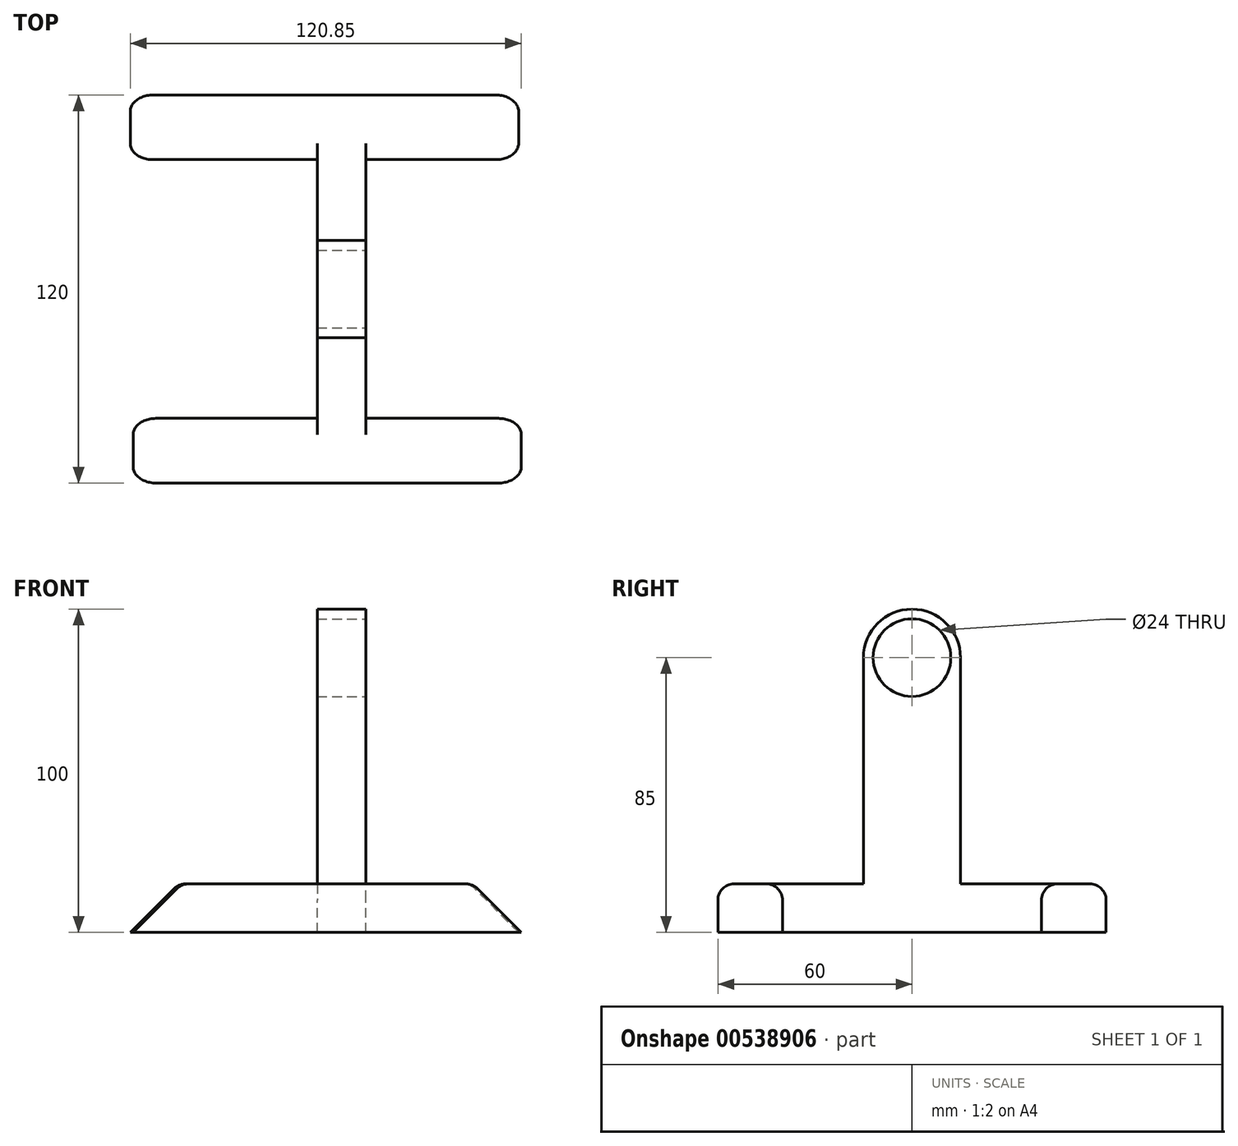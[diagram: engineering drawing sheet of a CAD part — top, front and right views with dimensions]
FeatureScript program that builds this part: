
annotation { "Feature Type Name" : "Feature", "Feature Type Description" : "" }
export const myFeature = defineFeature(function(context is Context, id is Id, definition is map)
    precondition{}
    {
        {
            var Q0;
            Q0=qCreatedBy(makeId("Front.planeOp"),FACE);
            var sketch = newSketch(context, id + "F0", { "sketchPlane" : qUnion([Q0])});
            skLineSegment(sketch, "E0", {"start": v(-49.17, 0) * mm, "end": v(10.83, 0) * mm});
            skLineSegment(sketch, "E1", {"start": v(-49.17, 0) * mm, "end": v(-64.17, 0) * mm});
            skLineSegment(sketch, "E2", {"start": v(10.83, 0) * mm, "end": v(25.83, 0) * mm});
            skLineSegment(sketch, "E3", {"start": v(-49.17, -15) * mm, "end": v(10.83, -15) * mm});
            skLineSegment(sketch, "E4", {"start": v(-49.17, -15) * mm, "end": v(-79.17, -15) * mm});
            skLineSegment(sketch, "E5", {"start": v(10.83, -15) * mm, "end": v(40.83, -15) * mm});
            skLineSegment(sketch, "E6", {"start": v(-64.17, 0) * mm, "end": v(-79.17, -15) * mm});
            skLineSegment(sketch, "E7", {"start": v(25.83, 0) * mm, "end": v(40.83, -15) * mm});
            skLineSegment(sketch, "E8", {"start": v(-49.17, 0) * mm, "end": v(-19.17, 0) * mm});
            skLineSegment(sketch, "E9", {"start": v(-19.17, 0) * mm, "end": v(10.83, 0) * mm});
            skSolve(sketch);
        }
        {
            var Q0;
            Q0 = qSketchRegion(id + "F0", true);
            extrude(context, id + "F1", {"entities" : qUnion([Q0]), "depth" : 20 * mm, "offsetDistance" : 25 * mm});
        }
        {
            var Q0;
            Q0=makeQuery(id+"F1.opExtrude","CAP_FACE",FACE,{"disambiguationData":[OSD([sQuery(id+"F0.wireOp",EDGE,"E0"),sQuery(id+"F0.wireOp",EDGE,"E1"),sQuery(id+"F0.wireOp",EDGE,"E2"),sQuery(id+"F0.wireOp",EDGE,"E3"),sQuery(id+"F0.wireOp",EDGE,"E4"),sQuery(id+"F0.wireOp",EDGE,"E5"),sQuery(id+"F0.wireOp",EDGE,"E6"),sQuery(id+"F0.wireOp",EDGE,"E7")])],"isStart":true});
            var sketch = newSketch(context, id + "F2", { "sketchPlane" : qUnion([Q0])});
            skLineSegment(sketch, "E10.bottom", {"start": v(22.23, -15) * mm, "end": v(7.23, -15) * mm});
            skLineSegment(sketch, "E10.top", {"start": v(22.23, 0) * mm, "end": v(7.23, 0) * mm});
            skLineSegment(sketch, "E10.left", {"start": v(22.23, -15) * mm, "end": v(22.23, 0) * mm});
            skLineSegment(sketch, "E10.right", {"start": v(7.23, -15) * mm, "end": v(7.23, 0) * mm});
            skPoint(sketch, "E10.middle", {"position": v(14.73, -7.5) * mm});
            skSolve(sketch);
        }
        {
            var Q0;
            Q0 = qSketchRegion(id + "F2", true);
            extrude(context, id + "F3", {"entities" : qUnion([Q0]), "operationType" : NewBodyOperationType.ADD, "depth" : 80 * mm, "offsetDistance" : 25 * mm});
        }
        {
            var Q0;
            Q0=makeQuery(id+"F3.opExtrude","CAP_FACE",FACE,{"disambiguationData":[OSD([sQuery(id+"F2.wireOp",EDGE,"E10.bottom"),sQuery(id+"F2.wireOp",EDGE,"E10.top"),sQuery(id+"F2.wireOp",EDGE,"E10.left"),sQuery(id+"F2.wireOp",EDGE,"E10.right")])],"isStart":false});
            var sketch = newSketch(context, id + "F4", { "sketchPlane" : qUnion([Q0])});
            skLineSegment(sketch, "E11", {"start": v(-24.98, 0) * mm, "end": v(65.02, 0) * mm});
            skLineSegment(sketch, "E12", {"start": v(65.02, 0) * mm, "end": v(80.02, -15) * mm});
            skLineSegment(sketch, "E13", {"start": v(80.02, -15) * mm, "end": v(-39.98, -15) * mm});
            skLineSegment(sketch, "E14", {"start": v(-39.98, -15) * mm, "end": v(-24.98, 0) * mm});
            skLineSegment(sketch, "E15", {"start": v(-39.98, -15) * mm, "end": v(-19.98, -15) * mm});
            skLineSegment(sketch, "E16", {"start": v(80.02, -15) * mm, "end": v(60.02, -15) * mm});
            skLineSegment(sketch, "E17", {"start": v(-19.98, -15) * mm, "end": v(60.02, -15) * mm});
            skSolve(sketch);
        }
        {
            var Q0;
            {var subQ2=sQuery(id+"F4.wireOp",EDGE,"E14");Q0=makeQuery(id+"F4.imprint","IMPRINT",FACE,{"disambiguationData":[TD([[makeQuery(id+"F4.imprint","IMPRINT",EDGE,{"derivedFrom":subQ2}),-1.0]])]});}
            var Q1;
            {var subQ1=makeQuery(id+"F3.opExtrude","CAP_EDGE",EDGE,{"disambiguationData":[OSD([sQuery(id+"F2.wireOp",EDGE,"E10.left")])],"isStart":false});Q1=makeQuery(id+"F4.imprint","IMPRINT",FACE,{"disambiguationData":[TD([[makeQuery(id+"F4.imprint","IMPRINT",EDGE,{"derivedFrom":subQ1}),1.0]])]});}
            var Q2;
            {var subQ2=sQuery(id+"F4.wireOp",EDGE,"E12");Q2=makeQuery(id+"F4.imprint","IMPRINT",FACE,{"disambiguationData":[TD([[makeQuery(id+"F4.imprint","IMPRINT",EDGE,{"derivedFrom":subQ2}),-1.0]])]});}
            extrude(context, id + "F5", {"entities" : qUnion([Q0, Q1, Q2]), "operationType" : NewBodyOperationType.ADD, "depth" : 20 * mm, "offsetDistance" : 25 * mm});
        }
        {
            var Q0;
            Q0=makeQuery(id+"F5.opExtrude","SWEPT_EDGE",EDGE,{"disambiguationData":[OSD([sQuery(id+"F4.wireOp",EDGE,"E11"),sQuery(id+"F4.wireOp",EDGE,"E12")])]});
            var Q1;
            Q1=makeQuery(id+"F5.opExtrude","SWEPT_EDGE",EDGE,{"disambiguationData":[OSD([sQuery(id+"F4.wireOp",EDGE,"E11"),sQuery(id+"F4.wireOp",EDGE,"E14")])]});
            var Q2;
            Q2=makeQuery(id+"F1.opExtrude","SWEPT_EDGE",EDGE,{"disambiguationData":[OSD([sQuery(id+"F0.wireOp",EDGE,"E1"),sQuery(id+"F0.wireOp",EDGE,"E6")])]});
            var Q3;
            Q3=makeQuery(id+"F1.opExtrude","SWEPT_EDGE",EDGE,{"disambiguationData":[OSD([sQuery(id+"F0.wireOp",EDGE,"E2"),sQuery(id+"F0.wireOp",EDGE,"E7")])]});
            var Q4;
            {var subQ0=sQuery(id+"F0.wireOp",EDGE,"E6");var subQ1=sQuery(id+"F0.wireOp",EDGE,"E2");var subQ2=sQuery(id+"F0.wireOp",EDGE,"E1");var subQ3=sQuery(id+"F0.wireOp",EDGE,"E0");Q4=makeQuery(id+"F3.boolean.opBoolean","SPLIT",EDGE,{"disambiguationData":[TD([makeQuery(id+"F1.opExtrude","SWEPT_FACE",FACE,{"disambiguationData":[OSD([subQ0])]})])],"derivedFrom":makeQuery(id+"F1.opExtrude","CAP_EDGE",EDGE,{"disambiguationData":[OSD([subQ3,subQ2,subQ1])],"isStart":true})});}
            var Q5;
            {var subQ0=sQuery(id+"F0.wireOp",EDGE,"E7");var subQ1=sQuery(id+"F0.wireOp",EDGE,"E2");var subQ2=sQuery(id+"F0.wireOp",EDGE,"E1");var subQ3=sQuery(id+"F0.wireOp",EDGE,"E0");Q5=makeQuery(id+"F3.boolean.opBoolean","SPLIT",EDGE,{"disambiguationData":[TD([makeQuery(id+"F1.opExtrude","SWEPT_FACE",FACE,{"disambiguationData":[OSD([subQ0])]})])],"derivedFrom":makeQuery(id+"F1.opExtrude","CAP_EDGE",EDGE,{"disambiguationData":[OSD([subQ3,subQ2,subQ1])],"isStart":true})});}
            var Q6;
            Q6=makeQuery(id+"F1.opExtrude","CAP_EDGE",EDGE,{"disambiguationData":[OSD([sQuery(id+"F0.wireOp",EDGE,"E7")])],"isStart":true});
            var Q7;
            Q7=makeQuery(id+"F1.opExtrude","CAP_EDGE",EDGE,{"disambiguationData":[OSD([sQuery(id+"F0.wireOp",EDGE,"E6")])],"isStart":true});
            var Q8;
            Q8=makeQuery(id+"F1.opExtrude","CAP_EDGE",EDGE,{"disambiguationData":[OSD([sQuery(id+"F0.wireOp",EDGE,"E6")])],"isStart":false});
            var Q9;
            Q9=makeQuery(id+"F1.opExtrude","CAP_EDGE",EDGE,{"disambiguationData":[OSD([sQuery(id+"F0.wireOp",EDGE,"E0"),sQuery(id+"F0.wireOp",EDGE,"E1"),sQuery(id+"F0.wireOp",EDGE,"E2")])],"isStart":false});
            var Q10;
            Q10=makeQuery(id+"F1.opExtrude","CAP_EDGE",EDGE,{"disambiguationData":[OSD([sQuery(id+"F0.wireOp",EDGE,"E7")])],"isStart":false});
            var Q11;
            {var subQ0=sQuery(id+"F4.wireOp",EDGE,"E11");Q11=makeQuery(id+"F5.boolean.opBoolean","SPLIT",EDGE,{"disambiguationData":[TD([makeQuery(id+"F3.opExtrude","SWEPT_FACE",FACE,{"disambiguationData":[OSD([sQuery(id+"F2.wireOp",EDGE,"E10.right")])]})])],"derivedFrom":makeQuery(id+"F5.opExtrude","CAP_EDGE",EDGE,{"disambiguationData":[OSD([subQ0])],"isStart":true})});}
            var Q12;
            {var subQ0=sQuery(id+"F4.wireOp",EDGE,"E11");Q12=makeQuery(id+"F5.boolean.opBoolean","SPLIT",EDGE,{"disambiguationData":[TD([makeQuery(id+"F3.opExtrude","SWEPT_FACE",FACE,{"disambiguationData":[OSD([sQuery(id+"F2.wireOp",EDGE,"E10.left")])]})])],"derivedFrom":makeQuery(id+"F5.opExtrude","CAP_EDGE",EDGE,{"disambiguationData":[OSD([subQ0])],"isStart":true})});}
            var Q13;
            Q13=makeQuery(id+"F5.opExtrude","CAP_EDGE",EDGE,{"disambiguationData":[OSD([sQuery(id+"F4.wireOp",EDGE,"E12")])],"isStart":true});
            var Q14;
            Q14=makeQuery(id+"F5.opExtrude","CAP_EDGE",EDGE,{"disambiguationData":[OSD([sQuery(id+"F4.wireOp",EDGE,"E12")])],"isStart":false});
            var Q15;
            Q15=makeQuery(id+"F5.opExtrude","CAP_EDGE",EDGE,{"disambiguationData":[OSD([sQuery(id+"F4.wireOp",EDGE,"E11")])],"isStart":false});
            var Q16;
            Q16=makeQuery(id+"F5.opExtrude","CAP_EDGE",EDGE,{"disambiguationData":[OSD([sQuery(id+"F4.wireOp",EDGE,"E14")])],"isStart":false});
            var Q17;
            Q17=makeQuery(id+"F5.opExtrude","CAP_EDGE",EDGE,{"disambiguationData":[OSD([sQuery(id+"F4.wireOp",EDGE,"E14")])],"isStart":true});
            fillet(context, id + "F6", {"entities" : qUnion([Q0, Q1, Q2, Q3, Q4, Q5, Q6, Q7, Q8, Q9, Q10, Q11, Q12, Q13, Q14, Q15, Q16, Q17]), "radius" : 5 * mm, "tangentPropagation" : true, "allowEdgeOverflow" : false});
        }
        {
            var Q0;
            Q0=makeQuery(id+"F5.boolean.opBoolean","MERGE",FACE,{"derivedFrom":[makeQuery(id+"F3.boolean.opBoolean","MERGE",FACE,{"derivedFrom":[makeQuery(id+"F1.opExtrude","SWEPT_FACE",FACE,{"disambiguationData":[OSD([sQuery(id+"F0.wireOp",EDGE,"E0"),sQuery(id+"F0.wireOp",EDGE,"E1"),sQuery(id+"F0.wireOp",EDGE,"E2")])]}),makeQuery(id+"F3.opExtrude","SWEPT_FACE",FACE,{"disambiguationData":[OSD([sQuery(id+"F2.wireOp",EDGE,"E10.top")])]})]}),makeQuery(id+"F5.opExtrude","SWEPT_FACE",FACE,{"disambiguationData":[OSD([sQuery(id+"F4.wireOp",EDGE,"E11")])]})]});
            var sketch = newSketch(context, id + "F7", { "sketchPlane" : qUnion([Q0])});
            skLineSegment(sketch, "E18.bottom", {"start": v(-7.23, 25) * mm, "end": v(-22.23, 25) * mm});
            skLineSegment(sketch, "E18.top", {"start": v(-7.23, 55) * mm, "end": v(-22.23, 55) * mm});
            skLineSegment(sketch, "E18.left", {"start": v(-7.23, 25) * mm, "end": v(-7.23, 55) * mm});
            skLineSegment(sketch, "E18.right", {"start": v(-22.23, 25) * mm, "end": v(-22.23, 55) * mm});
            skPoint(sketch, "E18.middle", {"position": v(-14.73, 40) * mm});
            skLineSegment(sketch, "E19", {"start": v(-22.23, 55) * mm, "end": v(-22.23, 40) * mm});
            skLineSegment(sketch, "E20", {"start": v(-22.23, 40) * mm, "end": v(-22.23, 25) * mm});
            skSolve(sketch);
        }
        {
            var Q0;
            Q0=makeQuery(id+"F7.imprint","IMPRINT",FACE,{"disambiguationData":[TD([[makeQuery(id+"F7.imprint","IMPRINT",EDGE,{"derivedFrom":sQuery(id+"F7.wireOp",EDGE,"E18.bottom")}),-1.0]])]});
            extrude(context, id + "F8", {"entities" : qUnion([Q0]), "operationType" : NewBodyOperationType.ADD, "depth" : 85 * mm, "offsetDistance" : 25 * mm});
        }
        {
            var Q0;
            Q0=makeQuery(id+"F8.boolean.opBoolean","MERGE",FACE,{"derivedFrom":[makeQuery(id+"F3.opExtrude","SWEPT_FACE",FACE,{"disambiguationData":[OSD([sQuery(id+"F2.wireOp",EDGE,"E10.right")])]}),makeQuery(id+"F8.opExtrude","SWEPT_FACE",FACE,{"disambiguationData":[OSD([sQuery(id+"F7.wireOp",EDGE,"E18.left")])]})]});
            var sketch = newSketch(context, id + "F9", { "sketchPlane" : qUnion([Q0])});
            skLineSegment(sketch, "E21", {"start": v(40, 85) * mm, "end": v(40, 55) * mm});
            skCircle(sketch, "E22", {"center": v(40, 70) * mm, "radius": 15 * mm});
            skSolve(sketch);
        }
        {
            var Q0;
            {var subQ0=sQuery(id+"F9.wireOp",EDGE,"E22");var subQ1=sQuery(id+"F7.wireOp",EDGE,"E18.left");var subQ2=makeQuery(id+"F8.opExtrude","CAP_EDGE",EDGE,{"disambiguationData":[OSD([subQ1])],"isStart":false});var subQ3=makeQuery(id+"F9.imprint","INTERSECT",VERTEX,{"derivedFrom":[subQ2,sQuery(id+"F9.wireOp",EDGE,"E21"),subQ0]});Q0=makeQuery(id+"F9.imprint","IMPRINT",FACE,{"disambiguationData":[TD([[makeQuery(id+"F9.imprint","IMPRINT",EDGE,{"disambiguationData":[TD([[subQ3,-1.0]])],"derivedFrom":subQ0}),-1.0]])]});}
            var Q1;
            {var subQ0=sQuery(id+"F9.wireOp",EDGE,"E22");var subQ1=sQuery(id+"F7.wireOp",EDGE,"E18.left");var subQ2=makeQuery(id+"F8.opExtrude","CAP_EDGE",EDGE,{"disambiguationData":[OSD([subQ1])],"isStart":false});var subQ3=makeQuery(id+"F9.imprint","INTERSECT",VERTEX,{"derivedFrom":[subQ2,sQuery(id+"F9.wireOp",EDGE,"E21"),subQ0]});Q1=makeQuery(id+"F9.imprint","IMPRINT",FACE,{"disambiguationData":[TD([[makeQuery(id+"F9.imprint","IMPRINT",EDGE,{"disambiguationData":[TD([[subQ3,1.0]])],"derivedFrom":subQ0}),-1.0]])]});}
            extrude(context, id + "F10", {"entities" : qUnion([Q0, Q1]), "operationType" : NewBodyOperationType.REMOVE, "oppositeDirection" : true, "depth" : 25 * mm, "offsetDistance" : 25 * mm});
        }
        {
            var Q0;
            Q0=makeQuery(id+"F8.boolean.opBoolean","MERGE",FACE,{"derivedFrom":[makeQuery(id+"F3.opExtrude","SWEPT_FACE",FACE,{"disambiguationData":[OSD([sQuery(id+"F2.wireOp",EDGE,"E10.right")])]}),makeQuery(id+"F8.opExtrude","SWEPT_FACE",FACE,{"disambiguationData":[OSD([sQuery(id+"F7.wireOp",EDGE,"E18.left")])]})]});
            var sketch = newSketch(context, id + "F11", { "sketchPlane" : qUnion([Q0])});
            skCircle(sketch, "E23", {"center": v(40, 70) * mm, "radius": 12 * mm});
            skSolve(sketch);
        }
        {
            var Q0;
            Q0 = qSketchRegion(id + "F11", true);
            extrude(context, id + "F12", {"entities" : qUnion([Q0]), "operationType" : NewBodyOperationType.REMOVE, "endBound" : BoundingType.THROUGH_ALL, "oppositeDirection" : true, "depth" : 25 * mm, "offsetDistance" : 25 * mm});
        }
    });
